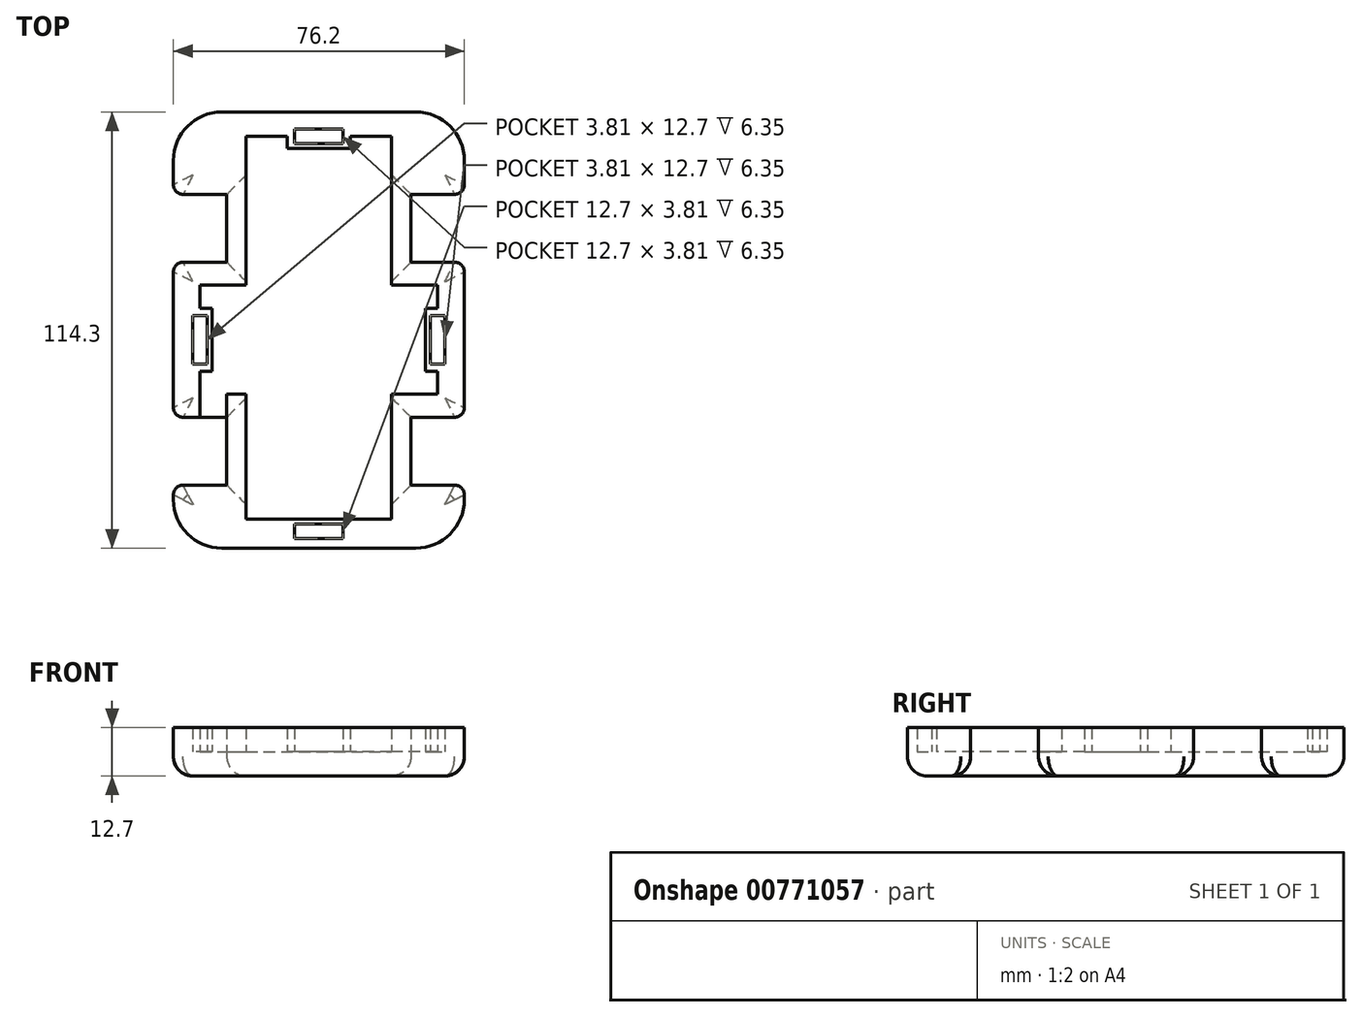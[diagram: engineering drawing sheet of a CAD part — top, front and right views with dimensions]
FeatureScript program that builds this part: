
annotation { "Feature Type Name" : "Feature", "Feature Type Description" : "" }
export const myFeature = defineFeature(function(context is Context, id is Id, definition is map)
    precondition{}
    {
        {
            var Q0;
            Q0=qCreatedBy(makeId("Top.planeOp"),FACE);
            var sketch = newSketch(context, id + "F0", { "sketchPlane" : qUnion([Q0])});
            skLineSegment(sketch, "E0.bottom", {"start": v(25.4, 57.15) * mm, "end": v(-25.4, 57.15) * mm});
            skLineSegment(sketch, "E0.top", {"start": v(25.4, -57.15) * mm, "end": v(-25.4, -57.15) * mm});
            skLineSegment(sketch, "E0.left", {"start": v(38.1, 44.45) * mm, "end": v(38.1, 38.1) * mm});
            skPoint(sketch, "E0.middle", {"position": v(0, 0) * mm});
            skLineSegment(sketch, "E1", {"start": v(0, 57.15) * mm, "end": v(0, 26.67) * mm, "construction": true});
            skLineSegment(sketch, "E2", {"start": v(0, 26.67) * mm, "end": v(0, 26.67) * mm});
            skLineSegment(sketch, "E3", {"start": v(-35.56, 35.56) * mm, "end": v(-24.13, 35.56) * mm});
            skLineSegment(sketch, "E4", {"start": v(-24.13, 35.56) * mm, "end": v(-24.13, 17.78) * mm});
            skLineSegment(sketch, "E5", {"start": v(-24.13, 17.78) * mm, "end": v(-35.56, 17.78) * mm});
            skLineSegment(sketch, "E6.MirrorCS", {"start": v(35.56, 35.56) * mm, "end": v(24.13, 35.56) * mm});
            skLineSegment(sketch, "E7.MirrorCS", {"start": v(24.13, 35.56) * mm, "end": v(24.13, 17.78) * mm});
            skLineSegment(sketch, "E8.MirrorCS", {"start": v(24.13, 17.78) * mm, "end": v(35.56, 17.78) * mm});
            skLineSegment(sketch, "E9", {"start": v(0, 26.67) * mm, "end": v(0, -2.54) * mm, "construction": true});
            skLineSegment(sketch, "E10", {"start": v(-62.39, -2.54) * mm, "end": v(58.62, -2.54) * mm, "construction": true});
            skLineSegment(sketch, "E11.MirrorCS", {"start": v(-24.13, -40.64) * mm, "end": v(-24.13, -22.86) * mm});
            skLineSegment(sketch, "E12.MirrorCS", {"start": v(-35.56, -40.64) * mm, "end": v(-24.13, -40.64) * mm});
            skLineSegment(sketch, "E13.MirrorCS", {"start": v(24.13, -22.86) * mm, "end": v(35.56, -22.86) * mm});
            skLineSegment(sketch, "E14.MirrorCS", {"start": v(24.13, -40.64) * mm, "end": v(24.13, -22.86) * mm});
            skLineSegment(sketch, "E15.MirrorCS", {"start": v(35.56, -40.64) * mm, "end": v(24.13, -40.64) * mm});
            skPoint(sketch, "E16.visualSharp", {"position": v(-38.1, -57.15) * mm});
            skArc(sketch, "E16.filletArc", {"start": v(-38.1, -44.45) * mm, "mid": v(-34.38, -53.43) * mm, "end": v(-25.4, -57.15) * mm});
            skPoint(sketch, "E17.visualSharp", {"position": v(38.1, -57.15) * mm});
            skArc(sketch, "E17.filletArc", {"start": v(25.4, -57.15) * mm, "mid": v(34.38, -53.43) * mm, "end": v(38.1, -44.45) * mm});
            skPoint(sketch, "E18.visualSharp", {"position": v(-38.1, 57.15) * mm});
            skArc(sketch, "E18.filletArc", {"start": v(-25.4, 57.15) * mm, "mid": v(-34.38, 53.43) * mm, "end": v(-38.1, 44.45) * mm});
            skPoint(sketch, "E19.visualSharp", {"position": v(38.1, 57.15) * mm});
            skArc(sketch, "E19.filletArc", {"start": v(38.1, 44.45) * mm, "mid": v(34.38, 53.43) * mm, "end": v(25.4, 57.15) * mm});
            skLineSegment(sketch, "E20", {"start": v(-38.1, -43.18) * mm, "end": v(-38.1, -44.45) * mm});
            skLineSegment(sketch, "E21", {"start": v(-38.1, 38.1) * mm, "end": v(-38.1, 44.45) * mm});
            skPoint(sketch, "E22.visualSharp", {"position": v(-38.1, -40.64) * mm});
            skArc(sketch, "E22.filletArc", {"start": v(-35.56, -40.64) * mm, "mid": v(-37.36, -41.38) * mm, "end": v(-38.1, -43.18) * mm});
            skPoint(sketch, "E23.visualSharp", {"position": v(-38.1, 17.78) * mm});
            skArc(sketch, "E23.filletArc", {"start": v(-35.56, 17.78) * mm, "mid": v(-37.36, 17.04) * mm, "end": v(-38.1, 15.24) * mm});
            skPoint(sketch, "E24.visualSharp", {"position": v(-38.1, 35.56) * mm});
            skArc(sketch, "E24.filletArc", {"start": v(-38.1, 38.1) * mm, "mid": v(-37.36, 36.3) * mm, "end": v(-35.56, 35.56) * mm});
            skPoint(sketch, "E25.newPointB", {"position": v(38.1, 35.56) * mm});
            skArc(sketch, "E25.filletArc", {"start": v(35.56, 35.56) * mm, "mid": v(37.36, 36.3) * mm, "end": v(38.1, 38.1) * mm});
            skLineSegment(sketch, "E26", {"start": v(38.1, 15.24) * mm, "end": v(38.1, -20.32) * mm});
            skLineSegment(sketch, "E27", {"start": v(38.1, -43.18) * mm, "end": v(38.1, -44.45) * mm});
            skPoint(sketch, "E28.visualSharp", {"position": v(38.1, -40.64) * mm});
            skArc(sketch, "E28.filletArc", {"start": v(38.1, -43.18) * mm, "mid": v(37.36, -41.38) * mm, "end": v(35.56, -40.64) * mm});
            skPoint(sketch, "E29.visualSharp", {"position": v(38.1, -22.86) * mm});
            skArc(sketch, "E29.filletArc", {"start": v(35.56, -22.86) * mm, "mid": v(37.36, -22.12) * mm, "end": v(38.1, -20.32) * mm});
            skPoint(sketch, "E30.visualSharp", {"position": v(38.1, 17.78) * mm});
            skArc(sketch, "E30.filletArc", {"start": v(38.1, 15.24) * mm, "mid": v(37.36, 17.04) * mm, "end": v(35.56, 17.78) * mm});
            skLineSegment(sketch, "E31", {"start": v(-38.1, 15.24) * mm, "end": v(-38.1, -20.32) * mm});
            skLineSegment(sketch, "E32", {"start": v(-35.56, -22.86) * mm, "end": v(-24.13, -22.86) * mm});
            skPoint(sketch, "E33.visualSharp", {"position": v(-38.1, -22.86) * mm});
            skArc(sketch, "E33.filletArc", {"start": v(-38.1, -20.32) * mm, "mid": v(-37.36, -22.12) * mm, "end": v(-35.56, -22.86) * mm});
            skSolve(sketch);
        }
        {
            var Q0;
            Q0=makeQuery(id+"F0.imprint","IMPRINT",FACE,{"disambiguationData":[TD([[makeQuery(id+"F0.imprint","IMPRINT",EDGE,{"derivedFrom":sQuery(id+"F0.wireOp",EDGE,"E0.bottom")}),1.0]])]});
            extrude(context, id + "F1", {"entities" : qUnion([Q0]), "depth" : 6.35 * mm, "offsetDistance" : 25.4 * mm});
        }
        {
            var Q0;
            Q0=makeQuery(id+"F1.opExtrude","CAP_FACE",FACE,{"disambiguationData":[OSD([sQuery(id+"F0.wireOp",EDGE,"E0.bottom"),sQuery(id+"F0.wireOp",EDGE,"E0.top"),sQuery(id+"F0.wireOp",EDGE,"E0.left"),sQuery(id+"F0.wireOp",EDGE,"E3"),sQuery(id+"F0.wireOp",EDGE,"E4"),sQuery(id+"F0.wireOp",EDGE,"E5"),sQuery(id+"F0.wireOp",EDGE,"E6.MirrorCS"),sQuery(id+"F0.wireOp",EDGE,"E7.MirrorCS"),sQuery(id+"F0.wireOp",EDGE,"E8.MirrorCS"),sQuery(id+"F0.wireOp",EDGE,"E11.MirrorCS"),sQuery(id+"F0.wireOp",EDGE,"E12.MirrorCS"),sQuery(id+"F0.wireOp",EDGE,"E13.MirrorCS"),sQuery(id+"F0.wireOp",EDGE,"E14.MirrorCS"),sQuery(id+"F0.wireOp",EDGE,"E15.MirrorCS"),sQuery(id+"F0.wireOp",EDGE,"E16.filletArc"),sQuery(id+"F0.wireOp",EDGE,"E17.filletArc"),sQuery(id+"F0.wireOp",EDGE,"E18.filletArc"),sQuery(id+"F0.wireOp",EDGE,"E19.filletArc"),sQuery(id+"F0.wireOp",EDGE,"E20"),sQuery(id+"F0.wireOp",EDGE,"E21"),sQuery(id+"F0.wireOp",EDGE,"E22.filletArc"),sQuery(id+"F0.wireOp",EDGE,"E23.filletArc"),sQuery(id+"F0.wireOp",EDGE,"E24.filletArc"),sQuery(id+"F0.wireOp",EDGE,"E25.filletArc"),sQuery(id+"F0.wireOp",EDGE,"E26"),sQuery(id+"F0.wireOp",EDGE,"E27"),sQuery(id+"F0.wireOp",EDGE,"E28.filletArc"),sQuery(id+"F0.wireOp",EDGE,"E29.filletArc"),sQuery(id+"F0.wireOp",EDGE,"E30.filletArc"),sQuery(id+"F0.wireOp",EDGE,"E31"),sQuery(id+"F0.wireOp",EDGE,"E32"),sQuery(id+"F0.wireOp",EDGE,"E33.filletArc")])],"isStart":false});
            var sketch = newSketch(context, id + "F2", { "sketchPlane" : qUnion([Q0])});
            skLineSegment(sketch, "E34.0", {"start": v(25.4, -57.15) * mm, "end": v(-25.4, -57.15) * mm});
            skLineSegment(sketch, "E35.0", {"start": v(-38.1, 15.24) * mm, "end": v(-38.1, -20.32) * mm});
            skLineSegment(sketch, "E36.0", {"start": v(38.1, 15.24) * mm, "end": v(38.1, -20.32) * mm});
            skLineSegment(sketch, "E37.0", {"start": v(25.4, 57.15) * mm, "end": v(-25.4, 57.15) * mm});
            skLineSegment(sketch, "E38", {"start": v(0, -57.15) * mm, "end": v(0, -48.36) * mm, "construction": true});
            skLineSegment(sketch, "E39.bottom", {"start": v(8.26, -55.93) * mm, "end": v(-8.26, -55.93) * mm});
            skLineSegment(sketch, "E39.top", {"start": v(8.26, -49.58) * mm, "end": v(-8.26, -49.58) * mm});
            skLineSegment(sketch, "E39.left", {"start": v(8.26, -55.93) * mm, "end": v(8.26, -49.58) * mm});
            skLineSegment(sketch, "E39.right", {"start": v(-8.26, -55.93) * mm, "end": v(-8.26, -49.58) * mm});
            skPoint(sketch, "E39.middle", {"position": v(0, -52.76) * mm});
            skLineSegment(sketch, "E40.MirrorCS", {"start": v(8.26, 47.62) * mm, "end": v(-8.26, 47.62) * mm});
            skLineSegment(sketch, "E41.MirrorCS", {"start": v(-8.26, 53.98) * mm, "end": v(-8.26, 47.62) * mm});
            skLineSegment(sketch, "E42.MirrorCS", {"start": v(8.26, 53.98) * mm, "end": v(-8.26, 53.98) * mm});
            skLineSegment(sketch, "E43.MirrorCS", {"start": v(8.26, 53.98) * mm, "end": v(8.26, 47.62) * mm});
            skLineSegment(sketch, "E44.0", {"start": v(-24.13, 17.78) * mm, "end": v(-35.56, 17.78) * mm});
            skLineSegment(sketch, "E45.0", {"start": v(-35.56, -22.86) * mm, "end": v(-24.13, -22.86) * mm});
            skLineSegment(sketch, "E46", {"start": v(-24.13, -22.86) * mm, "end": v(-24.13, -14.46) * mm});
            skLineSegment(sketch, "E47", {"start": v(-24.13, -22.86) * mm, "end": v(-31.12, -22.86) * mm});
            skLineSegment(sketch, "E48", {"start": v(-31.12, -22.86) * mm, "end": v(-31.12, -2.54) * mm, "construction": true});
            skLineSegment(sketch, "E49.bottom", {"start": v(-27.94, -10.8) * mm, "end": v(-34.3, -10.8) * mm});
            skLineSegment(sketch, "E49.top", {"start": v(-27.94, 5.72) * mm, "end": v(-34.3, 5.72) * mm});
            skLineSegment(sketch, "E49.left", {"start": v(-27.94, -10.8) * mm, "end": v(-27.94, 5.72) * mm});
            skLineSegment(sketch, "E49.right", {"start": v(-34.3, -10.8) * mm, "end": v(-34.3, 5.72) * mm});
            skPoint(sketch, "E49.middle", {"position": v(-31.12, -2.54) * mm});
            skLineSegment(sketch, "E50", {"start": v(0, 9.84) * mm, "end": v(0, -15.34) * mm, "construction": true});
            skLineSegment(sketch, "E51.MirrorCS", {"start": v(27.94, -10.8) * mm, "end": v(27.94, 5.72) * mm});
            skLineSegment(sketch, "E52.MirrorCS", {"start": v(34.3, -10.8) * mm, "end": v(34.3, 5.72) * mm});
            skLineSegment(sketch, "E53.MirrorCS", {"start": v(27.94, -10.8) * mm, "end": v(34.3, -10.8) * mm});
            skLineSegment(sketch, "E54.MirrorCS", {"start": v(27.94, 5.72) * mm, "end": v(34.3, 5.72) * mm});
            skLineSegment(sketch, "E55", {"start": v(0, 0) * mm, "end": v(-8.64, 0) * mm, "construction": true});
            skLineSegment(sketch, "E56.bottom", {"start": v(-29.21, -8.89) * mm, "end": v(-33.02, -8.89) * mm});
            skLineSegment(sketch, "E56.top", {"start": v(-29.21, 3.81) * mm, "end": v(-33.02, 3.81) * mm});
            skLineSegment(sketch, "E56.left", {"start": v(-29.21, -8.89) * mm, "end": v(-29.21, 3.81) * mm});
            skLineSegment(sketch, "E56.right", {"start": v(-33.02, -8.89) * mm, "end": v(-33.02, 3.81) * mm});
            skLineSegment(sketch, "E57.MirrorCS", {"start": v(29.21, 3.81) * mm, "end": v(33.02, 3.81) * mm});
            skLineSegment(sketch, "E58.MirrorCS", {"start": v(33.02, -8.89) * mm, "end": v(33.02, 3.81) * mm});
            skLineSegment(sketch, "E59.MirrorCS", {"start": v(29.21, -8.89) * mm, "end": v(29.21, 3.81) * mm});
            skLineSegment(sketch, "E60.MirrorCS", {"start": v(29.21, -8.89) * mm, "end": v(33.02, -8.89) * mm});
            skLineSegment(sketch, "E61.bottom", {"start": v(6.35, -54.66) * mm, "end": v(-6.35, -54.66) * mm});
            skLineSegment(sketch, "E61.top", {"start": v(6.35, -50.85) * mm, "end": v(-6.35, -50.85) * mm});
            skLineSegment(sketch, "E61.left", {"start": v(6.35, -54.66) * mm, "end": v(6.35, -50.85) * mm});
            skLineSegment(sketch, "E61.right", {"start": v(-6.35, -54.66) * mm, "end": v(-6.35, -50.85) * mm});
            skLineSegment(sketch, "E62.MirrorCS", {"start": v(6.35, 52.7) * mm, "end": v(6.35, 48.9) * mm});
            skLineSegment(sketch, "E63.MirrorCS", {"start": v(-6.35, 52.7) * mm, "end": v(-6.35, 48.9) * mm});
            skLineSegment(sketch, "E64.MirrorCS", {"start": v(6.35, 48.9) * mm, "end": v(-6.35, 48.9) * mm});
            skLineSegment(sketch, "E65.MirrorCS", {"start": v(6.35, 52.7) * mm, "end": v(-6.35, 52.7) * mm});
            skPoint(sketch, "E66.startSnap0", {"position": v(29.85, -40.64) * mm});
            skLineSegment(sketch, "E67", {"start": v(-31.12, -10.8) * mm, "end": v(-31.12, -22.86) * mm});
            skLineSegment(sketch, "E68", {"start": v(-31.12, -16.83) * mm, "end": v(-19.05, -16.83) * mm});
            skLineSegment(sketch, "E69", {"start": v(-19.05, -16.83) * mm, "end": v(-19.05, -49.58) * mm});
            skLineSegment(sketch, "E70", {"start": v(-31.12, 5.72) * mm, "end": v(-31.12, 17.78) * mm});
            skLineSegment(sketch, "E71", {"start": v(-31.12, 11.75) * mm, "end": v(-19.05, 11.75) * mm});
            skLineSegment(sketch, "E72", {"start": v(-19.05, 11.75) * mm, "end": v(-19.05, 50.8) * mm});
            skPoint(sketch, "E72.endSnap0", {"position": v(-8.26, 50.8) * mm});
            skLineSegment(sketch, "E73", {"start": v(-19.05, 50.8) * mm, "end": v(-8.26, 50.8) * mm});
            skLineSegment(sketch, "E74", {"start": v(-19.05, -49.58) * mm, "end": v(-8.26, -49.58) * mm});
            skLineSegment(sketch, "E75", {"start": v(31.12, -10.8) * mm, "end": v(31.12, -22.86) * mm});
            skLineSegment(sketch, "E76", {"start": v(31.12, -22.86) * mm, "end": v(31.12, -16.83) * mm});
            skLineSegment(sketch, "E77", {"start": v(31.12, -16.83) * mm, "end": v(19.05, -16.83) * mm});
            skPoint(sketch, "E77.endSnap0", {"position": v(19.05, -49.58) * mm});
            skLineSegment(sketch, "E78", {"start": v(19.05, -16.83) * mm, "end": v(19.05, -49.58) * mm});
            skLineSegment(sketch, "E79", {"start": v(8.26, -49.58) * mm, "end": v(19.05, -49.58) * mm});
            skLineSegment(sketch, "E80", {"start": v(31.12, 5.72) * mm, "end": v(31.12, 17.78) * mm});
            skLineSegment(sketch, "E81", {"start": v(31.12, 11.75) * mm, "end": v(19.05, 11.75) * mm});
            skLineSegment(sketch, "E82", {"start": v(19.05, 11.75) * mm, "end": v(19.05, 50.8) * mm});
            skPoint(sketch, "E82.endSnap0", {"position": v(8.26, 50.8) * mm});
            skLineSegment(sketch, "E83", {"start": v(19.05, 50.8) * mm, "end": v(8.26, 50.8) * mm});
            skSolve(sketch);
        }
        {
            var Q0;
            Q0=makeQuery(id+"F2.imprint","IMPRINT",FACE,{"disambiguationData":[TD([[makeQuery(id+"F2.imprint","IMPRINT",EDGE,{"derivedFrom":sQuery(id+"F2.wireOp",EDGE,"E35.0")}),1.0]])]});
            var Q1;
            Q1=makeQuery(id+"F2.imprint","IMPRINT",FACE,{"disambiguationData":[TD([[makeQuery(id+"F2.imprint","IMPRINT",EDGE,{"derivedFrom":sQuery(id+"F2.wireOp",EDGE,"E37.0")}),1.0]])]});
            var Q2;
            Q2=makeQuery(id+"F2.imprint","IMPRINT",FACE,{"disambiguationData":[TD([[makeQuery(id+"F2.imprint","IMPRINT",EDGE,{"derivedFrom":sQuery(id+"F2.wireOp",EDGE,"E36.0")}),-1.0]])]});
            var Q3;
            Q3=makeQuery(id+"F2.imprint","IMPRINT",FACE,{"disambiguationData":[TD([[makeQuery(id+"F2.imprint","IMPRINT",EDGE,{"derivedFrom":sQuery(id+"F2.wireOp",EDGE,"E34.0")}),-1.0]])]});
            var Q4;
            {var subQ3=sQuery(id+"F2.wireOp",EDGE,"E49.left");Q4=makeQuery(id+"F2.imprint","IMPRINT",FACE,{"disambiguationData":[TD([[makeQuery(id+"F2.imprint","IMPRINT",EDGE,{"derivedFrom":subQ3}),1.0]])]});}
            var Q5;
            {var subQ0=sQuery(id+"F2.wireOp",EDGE,"E47");Q5=makeQuery(id+"F2.imprint","IMPRINT",FACE,{"disambiguationData":[TD([[makeQuery(id+"F2.imprint","IMPRINT",EDGE,{"derivedFrom":subQ0}),1.0]])]});}
            var Q6;
            {var subQ3=sQuery(id+"F2.wireOp",EDGE,"E51.MirrorCS");Q6=makeQuery(id+"F2.imprint","IMPRINT",FACE,{"disambiguationData":[TD([[makeQuery(id+"F2.imprint","IMPRINT",EDGE,{"derivedFrom":subQ3}),-1.0]])]});}
            var Q7;
            Q7=makeQuery(id+"F2.imprint","IMPRINT",FACE,{"disambiguationData":[TD([[makeQuery(id+"F2.imprint","IMPRINT",EDGE,{"derivedFrom":sQuery(id+"F2.wireOp",EDGE,"E39.bottom")}),-1.0]])]});
            var Q8;
            {var subQ2=sQuery(id+"F2.wireOp",EDGE,"E40.MirrorCS");Q8=makeQuery(id+"F2.imprint","IMPRINT",FACE,{"disambiguationData":[TD([[makeQuery(id+"F2.imprint","IMPRINT",EDGE,{"derivedFrom":subQ2}),-1.0]])]});}
            extrude(context, id + "F3", {"entities" : qUnion([Q0, Q1, Q2, Q3, Q4, Q5, Q6, Q7, Q8]), "operationType" : NewBodyOperationType.ADD, "depth" : 6.35 * mm, "offsetDistance" : 25.4 * mm});
        }
        {
            var Q0;
            Q0=makeQuery(id+"F1.opExtrude","CAP_FACE",FACE,{"disambiguationData":[OSD([sQuery(id+"F0.wireOp",EDGE,"E0.bottom"),sQuery(id+"F0.wireOp",EDGE,"E0.top"),sQuery(id+"F0.wireOp",EDGE,"E0.left"),sQuery(id+"F0.wireOp",EDGE,"E3"),sQuery(id+"F0.wireOp",EDGE,"E4"),sQuery(id+"F0.wireOp",EDGE,"E5"),sQuery(id+"F0.wireOp",EDGE,"E6.MirrorCS"),sQuery(id+"F0.wireOp",EDGE,"E7.MirrorCS"),sQuery(id+"F0.wireOp",EDGE,"E8.MirrorCS"),sQuery(id+"F0.wireOp",EDGE,"E11.MirrorCS"),sQuery(id+"F0.wireOp",EDGE,"E12.MirrorCS"),sQuery(id+"F0.wireOp",EDGE,"E13.MirrorCS"),sQuery(id+"F0.wireOp",EDGE,"E14.MirrorCS"),sQuery(id+"F0.wireOp",EDGE,"E15.MirrorCS"),sQuery(id+"F0.wireOp",EDGE,"E16.filletArc"),sQuery(id+"F0.wireOp",EDGE,"E17.filletArc"),sQuery(id+"F0.wireOp",EDGE,"E18.filletArc"),sQuery(id+"F0.wireOp",EDGE,"E19.filletArc"),sQuery(id+"F0.wireOp",EDGE,"E20"),sQuery(id+"F0.wireOp",EDGE,"E21"),sQuery(id+"F0.wireOp",EDGE,"E22.filletArc"),sQuery(id+"F0.wireOp",EDGE,"E23.filletArc"),sQuery(id+"F0.wireOp",EDGE,"E24.filletArc"),sQuery(id+"F0.wireOp",EDGE,"E25.filletArc"),sQuery(id+"F0.wireOp",EDGE,"E26"),sQuery(id+"F0.wireOp",EDGE,"E27"),sQuery(id+"F0.wireOp",EDGE,"E28.filletArc"),sQuery(id+"F0.wireOp",EDGE,"E29.filletArc"),sQuery(id+"F0.wireOp",EDGE,"E30.filletArc"),sQuery(id+"F0.wireOp",EDGE,"E31"),sQuery(id+"F0.wireOp",EDGE,"E32"),sQuery(id+"F0.wireOp",EDGE,"E33.filletArc")])],"isStart":true});
            fillet(context, id + "F4", {"entities" : qUnion([Q0]), "radius" : 5.08 * mm, "tangentPropagation" : true, "allowEdgeOverflow" : false});
        }
    });
